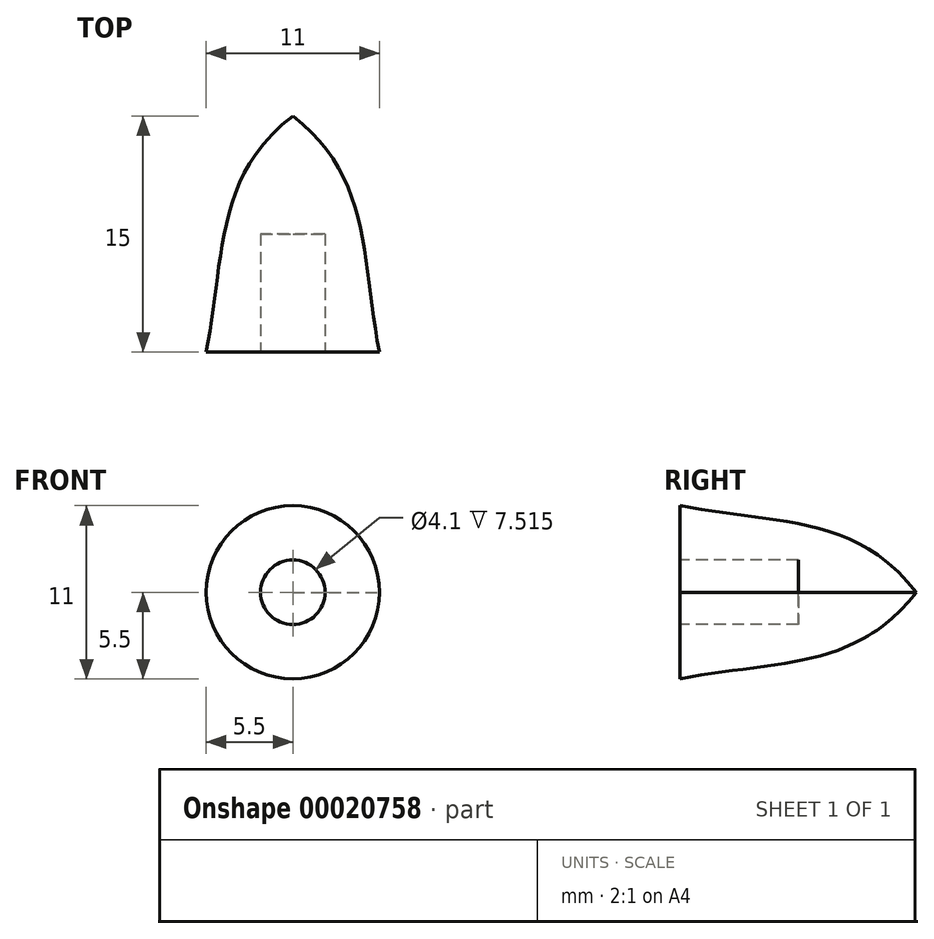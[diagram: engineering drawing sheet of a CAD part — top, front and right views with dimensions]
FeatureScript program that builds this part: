
annotation { "Feature Type Name" : "Feature", "Feature Type Description" : "" }
export const myFeature = defineFeature(function(context is Context, id is Id, definition is map)
    precondition{}
    {
        {
            var Q0;
            Q0=qCreatedBy(makeId("Top.planeOp"),FACE);
            var sketch = newSketch(context, id + "F0", { "sketchPlane" : qUnion([Q0])});
            skLineSegment(sketch, "E0.bottom", {"start": v(2.05, 0) * mm, "end": v(5.5, 0) * mm});
            skLineSegment(sketch, "E0.left", {"start": v(0, 7.51) * mm, "end": v(0, 15) * mm});
            skFitSpline(sketch, "E1", {"points": [v(0, 15) * mm, v(5.5, 0) * mm], "startDerivative": vector(15.14, -11.5) * mm, "endDerivative": vector(3.48, -17.32) * mm});
            skLineSegment(sketch, "E2.top", {"start": v(0, 7.51) * mm, "end": v(2.05, 7.51) * mm});
            skLineSegment(sketch, "E2.right", {"start": v(2.05, 0) * mm, "end": v(2.05, 7.51) * mm});
            skPoint(sketch, "E0.right.end.orphan", {"position": v(5.5, 15) * mm});
            skSolve(sketch);
        }
        {
            var Q0;
            Q0=makeQuery(id+"F0.imprint","IMPRINT",FACE,{"disambiguationData":[TD([[makeQuery(id+"F0.imprint","IMPRINT",EDGE,{"derivedFrom":sQuery(id+"F0.wireOp",EDGE,"E0.bottom")}),1.0]])]});
            var Q1;
            Q1=sQuery(id+"F0.wireOp",EDGE,"E0.left");
            revolve(context, id + "F1", {"entities" : qUnion([Q0]), "axis" : qUnion([Q1]), "revolveType" : RevolveType.FULL});
        }
    });
